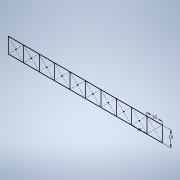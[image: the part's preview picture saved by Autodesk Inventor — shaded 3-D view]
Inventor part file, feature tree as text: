
AUTODESK INVENTOR PART (.ipt)
format: ipt  version: 2021 (Build 250183000, 183)  size: 106,496 bytes
history: native  units: mm
features: sketch x1
ambient origin geometry x8: Origin, YZ Plane, XZ Plane, XY Plane, X Axis, Y Axis, Z Axis, Center Point
feature tree (1):
  sketch  "Sketch1"  dims[d0=10.0mm d1=10.0mm d2=100.0mm d4=10.0mm d5=10.0mm d7=10.0mm]
